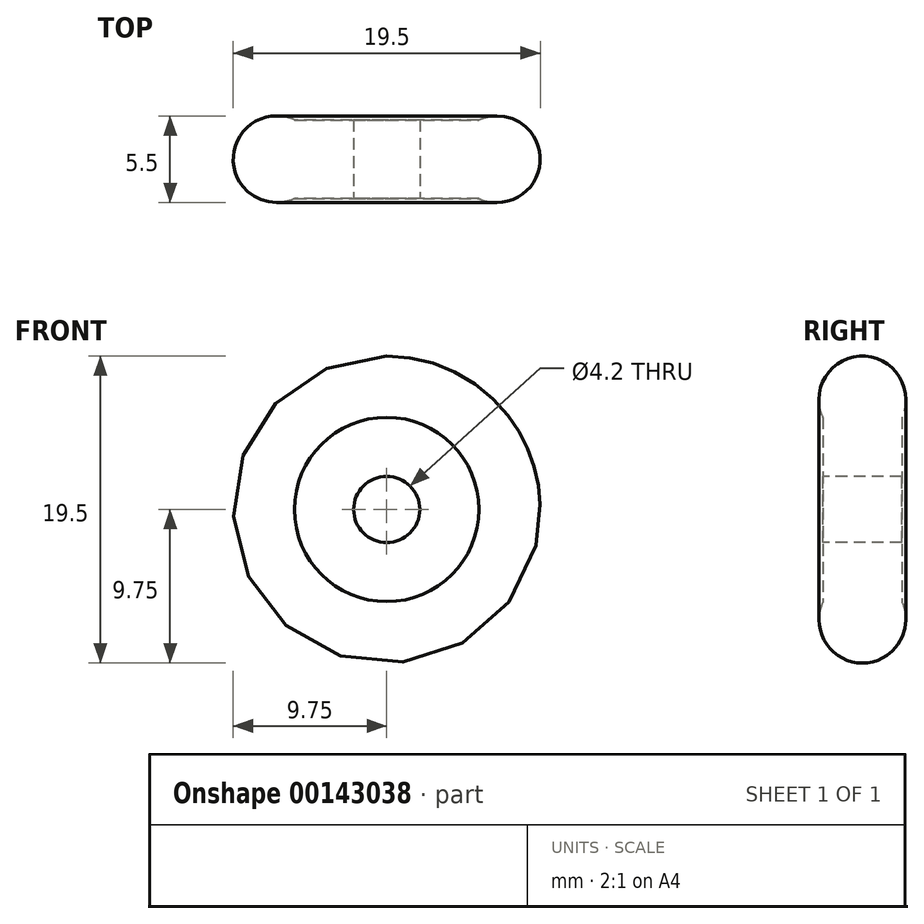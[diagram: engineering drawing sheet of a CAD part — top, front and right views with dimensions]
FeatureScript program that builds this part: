
annotation { "Feature Type Name" : "Feature", "Feature Type Description" : "" }
export const myFeature = defineFeature(function(context is Context, id is Id, definition is map)
    precondition{}
    {
        {
            var Q0;
            Q0=qCreatedBy(makeId("Front.planeOp"),FACE);
            var sketch = newSketch(context, id + "F0", { "sketchPlane" : qUnion([Q0])});
            skCircle(sketch, "E0", {"center": v(0, 0) * mm, "radius": 7 * mm});
            skSolve(sketch);
        }
        {
            var Q0;
            Q0 = qSketchRegion(id + "F0", true);
            extrude(context, id + "F1", {"entities" : qUnion([Q0]), "depth" : 5 * mm});
        }
        {
            var Q0;
            Q0=qCreatedBy(makeId("Top.planeOp"),FACE);
            var sketch = newSketch(context, id + "F2", { "sketchPlane" : qUnion([Q0])});
            skLineSegment(sketch, "E1", {"start": v(0, 0) * mm, "end": v(0, -5) * mm, "construction": true});
            skLineSegment(sketch, "E2", {"start": v(0, -2.5) * mm, "end": v(-7, -2.5) * mm, "construction": true});
            skCircle(sketch, "E3", {"center": v(-7, -2.5) * mm, "radius": 2.75 * mm});
            skSolve(sketch);
        }
        {
            var Q0;
            Q0 = qSketchRegion(id + "F2", true);
            var Q1;
            Q1=makeQuery(id+"F1.opExtrude","CAP_EDGE",EDGE,{"disambiguationData":[OSD([sQuery(id+"F0.wireOp",EDGE,"E0")])],"isStart":false});
            revolve(context, id + "F3", {"operationType" : NewBodyOperationType.ADD, "entities" : qUnion([Q0]), "axis" : qUnion([Q1]), "revolveType" : RevolveType.FULL});
        }
        {
            var Q0;
            Q0=makeQuery(id+"F1.opExtrude","CAP_FACE",FACE,{"disambiguationData":[OSD([sQuery(id+"F0.wireOp",EDGE,"E0")])],"isStart":false});
            var sketch = newSketch(context, id + "F4", { "sketchPlane" : qUnion([Q0])});
            skCircle(sketch, "E4", {"center": v(0, 0) * mm, "radius": 2.1 * mm});
            skSolve(sketch);
        }
        {
            var Q0;
            Q0 = qSketchRegion(id + "F4", true);
            extrude(context, id + "F5", {"entities" : qUnion([Q0]), "operationType" : NewBodyOperationType.REMOVE, "endBound" : BoundingType.THROUGH_ALL, "oppositeDirection" : true, "depth" : 25 * mm});
        }
    });
